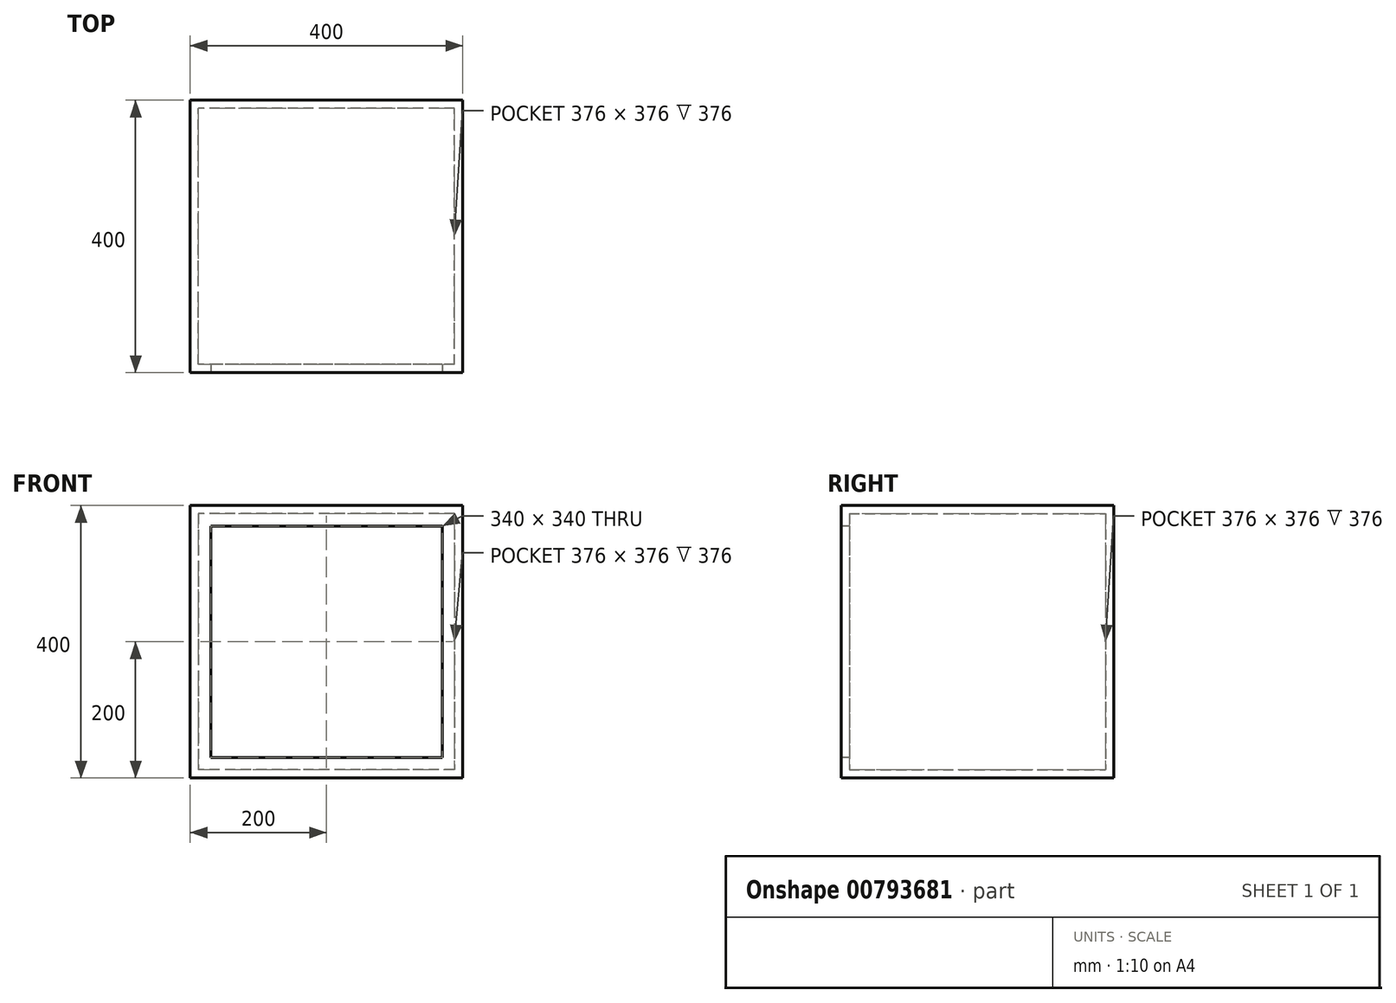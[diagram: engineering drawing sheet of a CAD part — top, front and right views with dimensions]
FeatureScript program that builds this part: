
annotation { "Feature Type Name" : "Feature", "Feature Type Description" : "" }
export const myFeature = defineFeature(function(context is Context, id is Id, definition is map)
    precondition{}
    {
        {
            var Q0;
            Q0=qCreatedBy(makeId("Top.planeOp"),FACE);
            var sketch = newSketch(context, id + "F0", { "sketchPlane" : qUnion([Q0])});
            skLineSegment(sketch, "E0.bottom", {"start": v(200, -200) * mm, "end": v(-200, -200) * mm});
            skLineSegment(sketch, "E0.top", {"start": v(200, 200) * mm, "end": v(-200, 200) * mm});
            skLineSegment(sketch, "E0.left", {"start": v(200, -200) * mm, "end": v(200, 200) * mm});
            skLineSegment(sketch, "E0.right", {"start": v(-200, -200) * mm, "end": v(-200, 200) * mm});
            skPoint(sketch, "E0.middle", {"position": v(0, 0) * mm});
            skSolve(sketch);
        }
        {
            var Q0;
            Q0 = qSketchRegion(id + "F0", true);
            extrude(context, id + "F1", {"entities" : qUnion([Q0]), "depth" : 400 * mm, "offsetDistance" : 25 * mm});
        }
        {
            var Q0;
            Q0=makeQuery(id+"F1.opExtrude","SWEPT_FACE",FACE,{"disambiguationData":[OSD([sQuery(id+"F0.wireOp",EDGE,"E0.bottom")])]});
            var sketch = newSketch(context, id + "F2", { "sketchPlane" : qUnion([Q0])});
            skLineSegment(sketch, "E1.bottom", {"start": v(170, 370) * mm, "end": v(-170, 370) * mm});
            skLineSegment(sketch, "E1.top", {"start": v(170, 30) * mm, "end": v(-170, 30) * mm});
            skLineSegment(sketch, "E1.left", {"start": v(170, 370) * mm, "end": v(170, 30) * mm});
            skLineSegment(sketch, "E1.right", {"start": v(-170, 370) * mm, "end": v(-170, 30) * mm});
            skPoint(sketch, "E1.middle", {"position": v(0, 200) * mm});
            skPoint(sketch, "E1.middle.positionSnap0", {"position": v(0, 400) * mm});
            skPoint(sketch, "E1.centerSnap0", {"position": v(0, 400) * mm});
            skSolve(sketch);
        }
        {
            var Q0;
            Q0 = qSketchRegion(id + "F2", true);
            extrude(context, id + "F3", {"entities" : qUnion([Q0]), "operationType" : NewBodyOperationType.REMOVE, "oppositeDirection" : true, "depth" : 12 * mm, "offsetDistance" : 25 * mm});
        }
        {
            var Q0;
            Q0=makeQuery(id+"F3.boolean.opBoolean","COPY",FACE,{"derivedFrom":makeQuery(id+"F3.opExtrude","CAP_FACE",FACE,{"disambiguationData":[OSD([sQuery(id+"F2.wireOp",EDGE,"E1.bottom"),sQuery(id+"F2.wireOp",EDGE,"E1.top"),sQuery(id+"F2.wireOp",EDGE,"E1.left"),sQuery(id+"F2.wireOp",EDGE,"E1.right")])],"isStart":false})});
            shell(context, id + "F4", {"entities" : qUnion([Q0]), "thickness" : 12 * mm});
        }
    });
